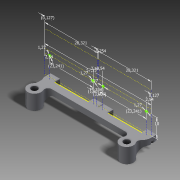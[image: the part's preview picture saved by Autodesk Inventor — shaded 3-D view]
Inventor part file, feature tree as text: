
AUTODESK INVENTOR PART (.ipt)
format: ipt  version: 2015 (Build 190159000, 159)  size: 367,104 bytes
history: native  units: in
note: dims shown in document units (in); Inventor stores cm internally (conversion verified against a paired STEP export)
features: sketch x8, extrude x7, pattern_linear x6, fillet x3, chamfer x2, projected_geometry x2
ambient origin geometry x8: Origin, YZ Plane, XZ Plane, XY Plane, X Axis, Y Axis, Z Axis, Center Point
bodies: Solid1 (feature_tree)
feature tree (28):
  extrude  "Extrusion1"  Depth=1.95in
  extrude  "Extrusion2"  Depth=0.2756in
  extrude  "Extrusion3"  Depth=0.1181in TaperAngle=0.0deg
  pattern_linear  "Rectangular Pattern1"  Spacing1=0.0394in  [1 undecoded]
  extrude  "Extrusion4"  Depth=0.0787in
  pattern_linear  "Rectangular Pattern2"  Spacing1=0.1181in  [1 undecoded]
  pattern_linear  "Rectangular Pattern3"  Spacing1=0.045in  [1 undecoded]
  extrude  "Extrusion5"  Depth=0.0787in TaperAngle=0.0deg
  extrude  "Extrusion6"  Depth=0.0787in
  pattern_linear  "Rectangular Pattern4"  Spacing1=0.0787in  [1 undecoded]
  pattern_linear  "Rectangular Pattern5"  Spacing1=0.0787in  [1 undecoded]
  pattern_linear  "Rectangular Pattern6"  Spacing1=0.025in  [1 undecoded]
  sketch  "Sketch8"  dims[d17=0.1575in]
  extrude  "Extrusion7"  Depth=0.0787in
  chamfer  "Chamfer1"  Distance=0.0956in
  chamfer  "Chamfer2"  Distance=0.7874in
  fillet  "Fillet2"  Radius=0.1181in
  fillet  "Fillet3"  Radius=0.7874in
  fillet  "Fillet4"  Radius=0.7874in
  sketch  "Sketch1"  dims[d0=0.1299in d2=1.95in]
  sketch  "Sketch2"  dims[d3=0.1299in d4=0.2756in]
  sketch  "Sketch3"  dims[d11=0.2756in d12=0.1181in d13=0.0in]
  sketch  "Sketch4"  dims[d14=0.2417in]
  sketch  "Sketch6"  dims[d15=0.0866in]
  sketch  "Sketch7"  dims[d16=0.1575in]
  projected_geometry  "Projected Loop1"
  projected_geometry  "Projected Loop2"
  sketch  "Sketch9"  dims[d18=0.0866in d19=0.0394in d20=0.0787in d21=0.1181in d22=0.0in d23=0.045in d24=0.1181in d25=0.0in d26=0.9094in d27=0.0787in d28=0.0787in d29=0.025in d30=0.025in d31=0.0956in d32=0.7874in d34=0.915in d35=0.1181in d36=0.0in d37=0.7874in d39=0.21in d40=0.7874in d42=1.125in d43=0.1181in d44=0.0in d46=0.0472in d47=0.0in d48=0.7874in d50=0.915in d51=0.7874in d53=1.125in d54=0.7874in d56=2.04in d57=2.25in d58=0.3937in d59=1.115in d60=0.005in d61=1.115in d62=0.01in d63=0.005in d64=0.05in d65=0.1in d66=0.05in d67=0.1in d68=0.05in d69=0.05in d70=0.1in d71=0.1in d72=0.915in d73=0.21in d74=0.915in d75=0.0656in d76=0.1444in d77=0.1969in d78=0.0in d79=0.1181in d80=0.0787in d81=45.0deg d82=0.1181in d83=0.0787in d84=45.0deg d86=0.0787in d87=0.0787in d88=0.0787in]
note: 6 required parameter values undecoded (feature->parameter linkage not recoverable at this tier; creation-order binding heuristic only, values carry confidence <= 0.55)
